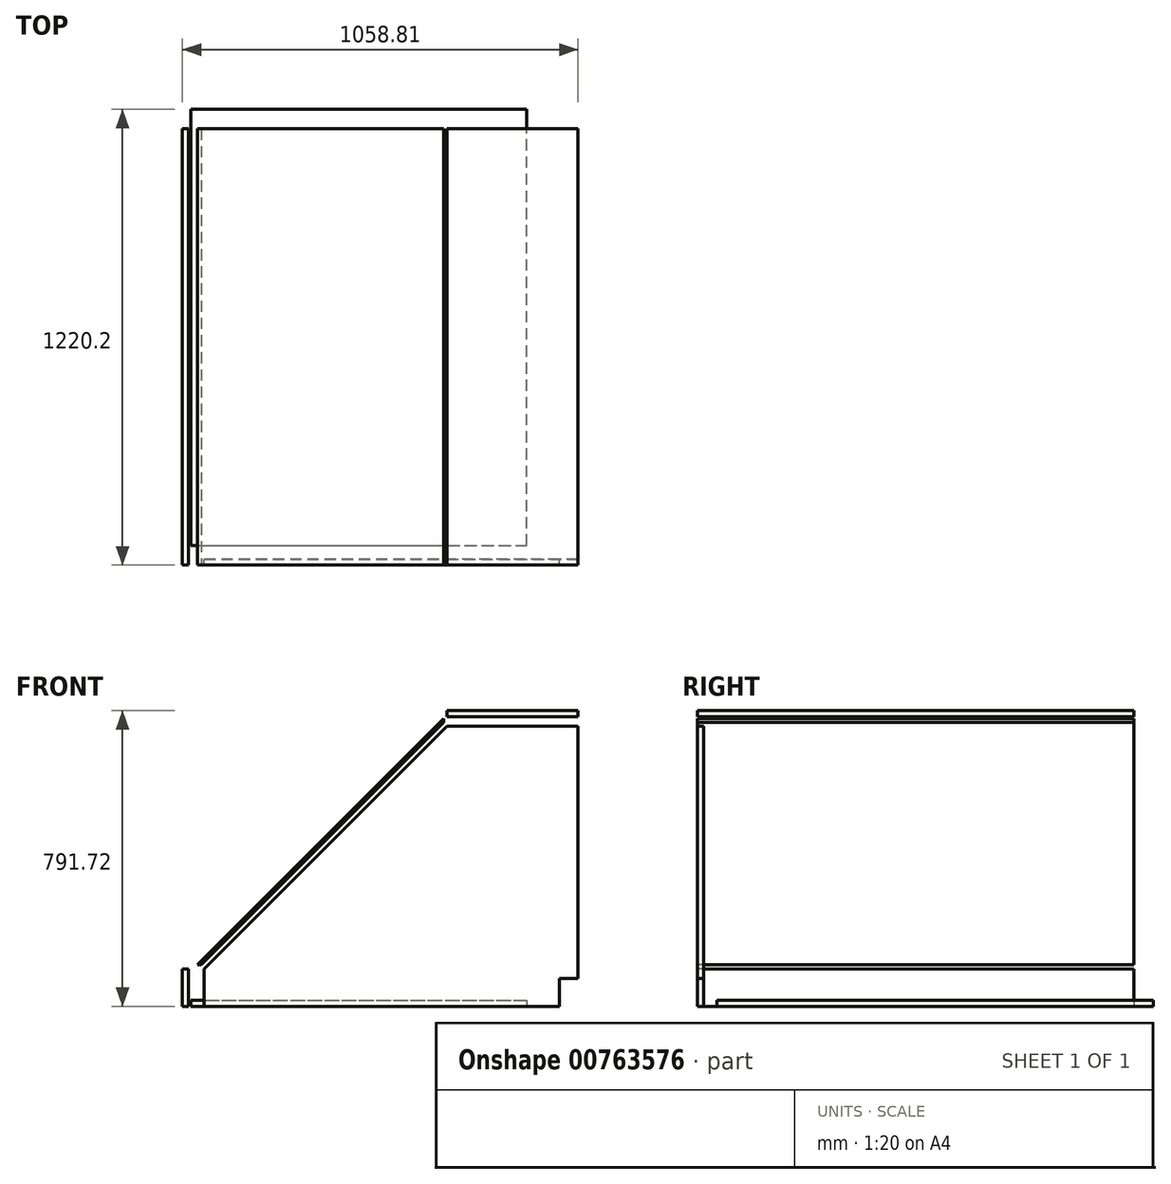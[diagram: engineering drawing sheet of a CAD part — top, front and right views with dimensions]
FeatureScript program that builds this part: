
annotation { "Feature Type Name" : "Feature", "Feature Type Description" : "" }
export const myFeature = defineFeature(function(context is Context, id is Id, definition is map)
    precondition{}
    {
        {
            var Q0;
            Q0=qCreatedBy(makeId("Front.planeOp"),FACE);
            var sketch = newSketch(context, id + "F0", { "sketchPlane" : qUnion([Q0])});
            skLineSegment(sketch, "E0", {"start": v(-1000, 0) * mm, "end": v(-1000, 100) * mm});
            skLineSegment(sketch, "E1", {"start": v(-1000, 100) * mm, "end": v(-350, 750) * mm});
            skLineSegment(sketch, "E2", {"start": v(-350, 750) * mm, "end": v(0, 750) * mm});
            skLineSegment(sketch, "E3", {"start": v(0, 750) * mm, "end": v(0, 75) * mm});
            skLineSegment(sketch, "E4", {"start": v(0, 75) * mm, "end": v(-50, 75) * mm});
            skLineSegment(sketch, "E5", {"start": v(-50, 75) * mm, "end": v(-50, 0) * mm});
            skLineSegment(sketch, "E6", {"start": v(-50, 0) * mm, "end": v(-1000, 0) * mm});
            skSolve(sketch);
        }
        {
            var Q0;
            Q0=makeQuery(id+"F0.imprint","IMPRINT",FACE,{"disambiguationData":[TD([[makeQuery(id+"F0.imprint","IMPRINT",EDGE,{"derivedFrom":sQuery(id+"F0.wireOp",EDGE,"E0")}),-1.0]])]});
            extrude(context, id + "F1", {"entities" : qUnion([Q0]), "depth" : 16 * mm, "offsetDistance" : 25 * mm});
        }
        {
            var Q0;
            Q0=qCreatedBy(makeId("Top.planeOp"),FACE);
            var sketch = newSketch(context, id + "F2", { "sketchPlane" : qUnion([Q0])});
            skLineSegment(sketch, "E7.bottom", {"start": v(-1036.58, 36.2) * mm, "end": v(-136.58, 36.2) * mm});
            skLineSegment(sketch, "E7.top", {"start": v(-1036.58, 1204.2) * mm, "end": v(-136.58, 1204.2) * mm});
            skLineSegment(sketch, "E7.left", {"start": v(-1036.58, 36.2) * mm, "end": v(-1036.58, 1204.2) * mm});
            skLineSegment(sketch, "E7.right", {"start": v(-136.58, 36.2) * mm, "end": v(-136.58, 1204.2) * mm});
            skSolve(sketch);
        }
        {
            var Q0;
            Q0=makeQuery(id+"F2.imprint","IMPRINT",FACE,{"disambiguationData":[TD([[makeQuery(id+"F2.imprint","IMPRINT",EDGE,{"derivedFrom":sQuery(id+"F2.wireOp",EDGE,"E7.bottom")}),1.0]])]});
            extrude(context, id + "F3", {"entities" : qUnion([Q0]), "depth" : 16 * mm, "offsetDistance" : 25 * mm});
        }
        {
            var Q0;
            Q0=makeQuery(id+"F1.opExtrude","CAP_FACE",FACE,{"disambiguationData":[OSD([sQuery(id+"F0.wireOp",EDGE,"E0"),sQuery(id+"F0.wireOp",EDGE,"E1"),sQuery(id+"F0.wireOp",EDGE,"E2"),sQuery(id+"F0.wireOp",EDGE,"E3"),sQuery(id+"F0.wireOp",EDGE,"E4"),sQuery(id+"F0.wireOp",EDGE,"E5"),sQuery(id+"F0.wireOp",EDGE,"E6")])],"isStart":false});
            var sketch = newSketch(context, id + "F4", { "sketchPlane" : qUnion([Q0])});
            skLineSegment(sketch, "E8.bottom", {"start": v(-350, 791.72) * mm, "end": v(0, 791.72) * mm});
            skLineSegment(sketch, "E8.top", {"start": v(-350, 775.72) * mm, "end": v(0, 775.72) * mm});
            skLineSegment(sketch, "E8.left", {"start": v(-350, 791.72) * mm, "end": v(-350, 775.72) * mm});
            skLineSegment(sketch, "E8.right", {"start": v(0, 791.72) * mm, "end": v(0, 775.72) * mm});
            skSolve(sketch);
        }
        {
            var Q0;
            Q0=makeQuery(id+"F4.imprint","IMPRINT",FACE,{"disambiguationData":[TD([[makeQuery(id+"F4.imprint","IMPRINT",EDGE,{"derivedFrom":sQuery(id+"F4.wireOp",EDGE,"E8.bottom")}),-1.0]])]});
            extrude(context, id + "F5", {"entities" : qUnion([Q0]), "oppositeDirection" : true, "depth" : 1168 * mm, "offsetDistance" : 25 * mm});
        }
        {
            var Q0;
            Q0=makeQuery(id+"F1.opExtrude","CAP_FACE",FACE,{"disambiguationData":[OSD([sQuery(id+"F0.wireOp",EDGE,"E0"),sQuery(id+"F0.wireOp",EDGE,"E1"),sQuery(id+"F0.wireOp",EDGE,"E2"),sQuery(id+"F0.wireOp",EDGE,"E3"),sQuery(id+"F0.wireOp",EDGE,"E4"),sQuery(id+"F0.wireOp",EDGE,"E5"),sQuery(id+"F0.wireOp",EDGE,"E6")])],"isStart":false});
            var sketch = newSketch(context, id + "F6", { "sketchPlane" : qUnion([Q0])});
            skLineSegment(sketch, "E9.bottom", {"start": v(-1058.81, 100) * mm, "end": v(-1042.81, 100) * mm});
            skLineSegment(sketch, "E9.top", {"start": v(-1058.81, 0) * mm, "end": v(-1042.81, 0) * mm});
            skLineSegment(sketch, "E9.left", {"start": v(-1058.81, 100) * mm, "end": v(-1058.81, 0) * mm});
            skLineSegment(sketch, "E9.right", {"start": v(-1042.81, 100) * mm, "end": v(-1042.81, 0) * mm});
            skSolve(sketch);
        }
        {
            var Q0;
            Q0 = qSketchRegion(id + "F6", true);
            extrude(context, id + "F7", {"entities" : qUnion([Q0]), "oppositeDirection" : true, "depth" : 1168 * mm, "offsetDistance" : 25 * mm});
        }
        {
            var Q0;
            Q0=makeQuery(id+"F1.opExtrude","CAP_FACE",FACE,{"disambiguationData":[OSD([sQuery(id+"F0.wireOp",EDGE,"E0"),sQuery(id+"F0.wireOp",EDGE,"E1"),sQuery(id+"F0.wireOp",EDGE,"E2"),sQuery(id+"F0.wireOp",EDGE,"E3"),sQuery(id+"F0.wireOp",EDGE,"E4"),sQuery(id+"F0.wireOp",EDGE,"E5"),sQuery(id+"F0.wireOp",EDGE,"E6")])],"isStart":false});
            var sketch = newSketch(context, id + "F8", { "sketchPlane" : qUnion([Q0])});
            skLineSegment(sketch, "E10", {"start": v(-359.89, 759.86) * mm, "end": v(-1008.55, 111.2) * mm});
            skLineSegment(sketch, "E11", {"start": v(-1008.55, 111.2) * mm, "end": v(-1018.8, 111.2) * mm});
            skLineSegment(sketch, "E12", {"start": v(-1018.8, 111.2) * mm, "end": v(-359.89, 770.1) * mm});
            skLineSegment(sketch, "E13", {"start": v(-359.89, 770.1) * mm, "end": v(-359.89, 759.86) * mm});
            skSolve(sketch);
        }
        {
            var Q0;
            Q0 = qSketchRegion(id + "F8", true);
            var Q1;
            Q1 = qConstructionFilter(qBodyType(qCreatedBy(id + "F8" ,EDGE), BodyType.WIRE), ConstructionObject.NO);
            extrude(context, id + "F9", {"entities" : qUnion([Q0]), "surfaceEntities" : qUnion([Q1]), "oppositeDirection" : true, "depth" : 1168 * mm, "offsetDistance" : 25 * mm});
        }
    });
